# Revit family: Safety-Railing_DockGate_SafetyRail_Roller-Gate
name_source: partatom
category: Railings
units: mm (PartAtom-declared; Revit-internal decimal feet)

## family parameters
Classification Number = 23.30.80.11
Cut with Voids When Loaded = No
Shared = No

## types (9) — shared parameters
Construction Details = http://www.arcat.com
Description = Safety Rail Company Loading Dock Roller Safety Gate - as Specified
Green Building-LEED = http://www.arcat.com
Keynote = 05 52 00
Manufacturer = Safety Rail Company
Manufacturer Fax = 888-471-4931
Manufacturer Website = http://www.safetyrailcompany.com
Model = Dock Roller Gate
Post OD = 0' - 4 3/32"
Product Data = http://www.arcat.com
Product Properties = http://www.safetyrailcompany.com
Revision = R1_2017-08
Sales Information = http://www.safetyrailcompany.com
SpecWizard = http://www.arcat.com
Specification = http://www.arcat.com
Standards Conformance = as Specified
URL = http://www.safetyrailcompany.com
Unit Height = 3' - 6 1/2"
zero-valued in all types: Expected Lifespan (Years), Maintenance Schedule (Months), Warranty Duration (Years)

## per-type parameters (varying)
| type | Clear Opening Width | Gate Length | Unit Length |
| 12 ft | 12' - 0" | 13' - 4" | 12' - 10" |
| 11 ft | 11' - 0" | 12' - 4" | 11' - 10" |
| 10 ft | 10' - 0" | 11' - 4" | 10' - 10" |
| 9 ft | 9' - 0" | 10' - 4" | 9' - 10" |
| 8 ft | 8' - 0" | 9' - 4" | 8' - 10" |
| 7 ft | 7' - 0" | 8' - 4" | 7' - 10" |
| 6 ft | 6' - 0" | 7' - 4" | 6' - 10" |
| 5 ft | 5' - 0" | 6' - 4" | 5' - 10" |
| 4 ft | 4' - 0" | 5' - 4" | 4' - 10" |

## geometry (parser evidence)
native form markers: Sweep x4
no freeform markers — native parametric forms only
